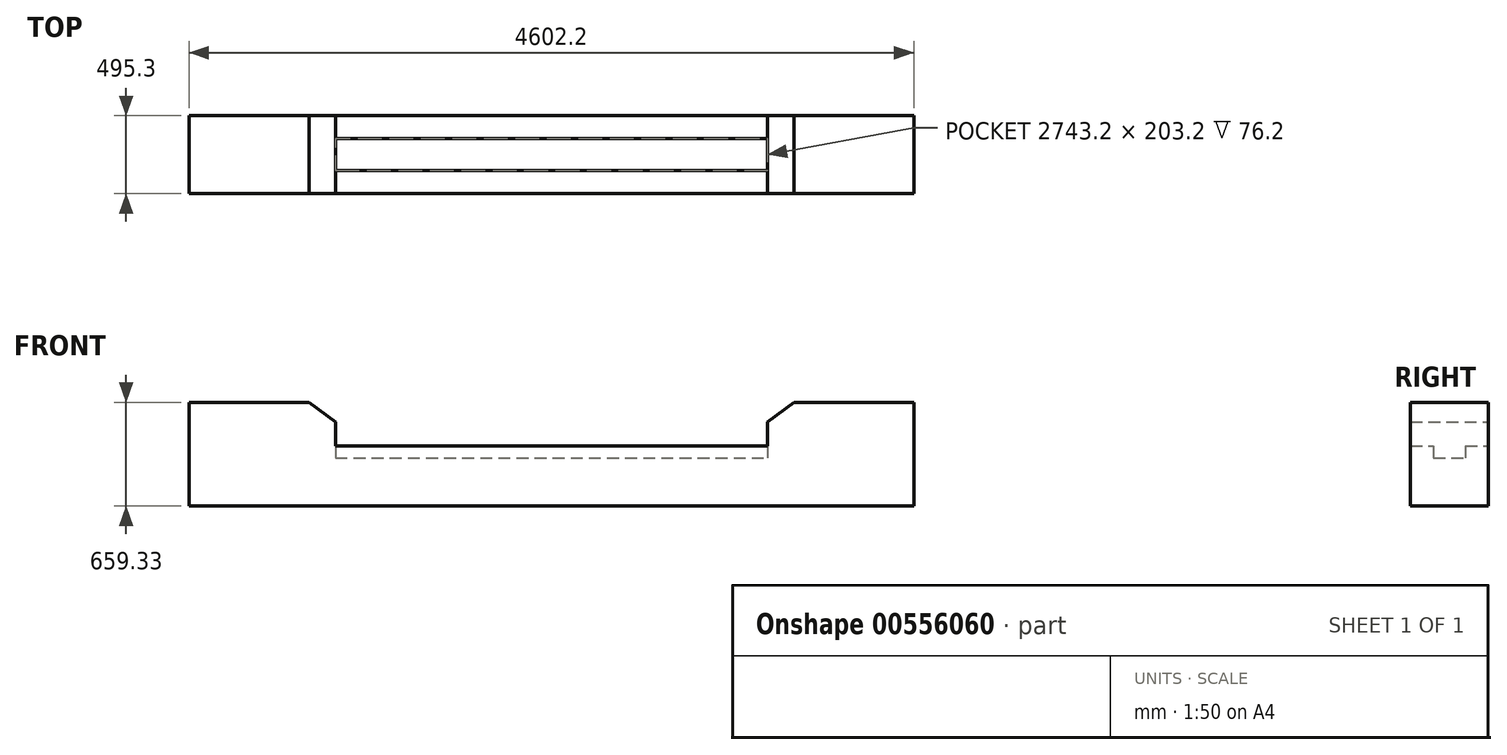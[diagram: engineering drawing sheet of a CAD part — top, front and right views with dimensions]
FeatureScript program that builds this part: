
annotation { "Feature Type Name" : "Feature", "Feature Type Description" : "" }
export const myFeature = defineFeature(function(context is Context, id is Id, definition is map)
    precondition{}
    {
        {
            var Q0;
            Q0=qCreatedBy(makeId("Front.planeOp"),FACE);
            var sketch = newSketch(context, id + "F0", { "sketchPlane" : qUnion([Q0])});
            skLineSegment(sketch, "E0", {"start": v(0, 0) * mm, "end": v(1371.6, 0) * mm});
            skLineSegment(sketch, "E1", {"start": v(1371.6, 0) * mm, "end": v(1371.6, -127) * mm});
            skLineSegment(sketch, "E2", {"start": v(1371.6, -127) * mm, "end": v(-1371.6, -127) * mm});
            skLineSegment(sketch, "E3", {"start": v(-1371.6, -127) * mm, "end": v(-1371.6, 0) * mm});
            skLineSegment(sketch, "E4", {"start": v(-1371.6, 0) * mm, "end": v(0, 0) * mm});
            skLineSegment(sketch, "E5", {"start": v(-1371.6, 101.6) * mm, "end": v(-1539.1, 227.53) * mm});
            skLineSegment(sketch, "E6", {"start": v(-1539.1, 227.53) * mm, "end": v(-2301.1, 227.53) * mm});
            skLineSegment(sketch, "E7", {"start": v(-2301.1, 227.53) * mm, "end": v(-2301.1, -229.67) * mm});
            skLineSegment(sketch, "E8", {"start": v(0, -127) * mm, "end": v(0, -431.8) * mm});
            skPoint(sketch, "E8.endSnap0", {"position": v(0, -127) * mm});
            skLineSegment(sketch, "E9", {"start": v(0, -431.8) * mm, "end": v(-2301.1, -431.8) * mm});
            skLineSegment(sketch, "E10", {"start": v(-2301.1, -431.8) * mm, "end": v(-2301.1, -229.67) * mm});
            skLineSegment(sketch, "E11.MirrorCS", {"start": v(0, -431.8) * mm, "end": v(2301.1, -431.8) * mm});
            skLineSegment(sketch, "E12.MirrorCS", {"start": v(2301.1, 227.53) * mm, "end": v(2301.1, -229.67) * mm});
            skLineSegment(sketch, "E13.MirrorCS", {"start": v(2301.1, -431.8) * mm, "end": v(2301.1, -229.67) * mm});
            skLineSegment(sketch, "E14.MirrorCS", {"start": v(1539.1, 227.53) * mm, "end": v(2301.1, 227.53) * mm});
            skLineSegment(sketch, "E15.MirrorCS", {"start": v(1371.6, 101.6) * mm, "end": v(1539.1, 227.53) * mm});
            skLineSegment(sketch, "E16.MirrorCS", {"start": v(1371.6, 0) * mm, "end": v(1371.6, 101.6) * mm});
            skLineSegment(sketch, "E17", {"start": v(-1371.6, 0) * mm, "end": v(-1371.6, 101.6) * mm});
            skSolve(sketch);
        }
        {
            var Q0;
            {var subQ0=sQuery(id+"F0.wireOp",EDGE,"E3");Q0=makeQuery(id+"F0.imprint","IMPRINT",FACE,{"disambiguationData":[TD([[makeQuery(id+"F0.imprint","IMPRINT",EDGE,{"derivedFrom":subQ0}),1.0]])]});}
            var Q1;
            {var subQ1=sQuery(id+"F0.wireOp",EDGE,"E1");Q1=makeQuery(id+"F0.imprint","IMPRINT",FACE,{"disambiguationData":[TD([[makeQuery(id+"F0.imprint","IMPRINT",EDGE,{"derivedFrom":subQ1}),1.0]])]});}
            extrude(context, id + "F1", {"entities" : qUnion([Q0, Q1]), "depth" : 349.25 * mm, "offsetDistance" : 25.4 * mm});
        }
        {
            var Q0;
            Q0=makeQuery(id+"F1.opExtrude","CAP_FACE",FACE,{"disambiguationData":[OSD([sQuery(id+"F0.wireOp",EDGE,"E1"),sQuery(id+"F0.wireOp",EDGE,"E2"),sQuery(id+"F0.wireOp",EDGE,"E3"),sQuery(id+"F0.wireOp",EDGE,"E5"),sQuery(id+"F0.wireOp",EDGE,"E6"),sQuery(id+"F0.wireOp",EDGE,"E7"),sQuery(id+"F0.wireOp",EDGE,"E9"),sQuery(id+"F0.wireOp",EDGE,"E10"),sQuery(id+"F0.wireOp",EDGE,"E11.MirrorCS"),sQuery(id+"F0.wireOp",EDGE,"E12.MirrorCS"),sQuery(id+"F0.wireOp",EDGE,"E13.MirrorCS"),sQuery(id+"F0.wireOp",EDGE,"E14.MirrorCS"),sQuery(id+"F0.wireOp",EDGE,"E15.MirrorCS"),sQuery(id+"F0.wireOp",EDGE,"E16.MirrorCS"),sQuery(id+"F0.wireOp",EDGE,"E17")])],"isStart":true});
            extrude(context, id + "F2", {"entities" : qUnion([Q0]), "operationType" : NewBodyOperationType.ADD, "depth" : 146.05 * mm, "offsetDistance" : 25.4 * mm});
        }
        {
            var Q0;
            {var subQ0=sQuery(id+"F0.wireOp",EDGE,"E2");Q0=makeQuery(id+"F2.boolean.opBoolean","MERGE",FACE,{"derivedFrom":[makeQuery(id+"F1.opExtrude","SWEPT_FACE",FACE,{"disambiguationData":[OSD([subQ0])]}),makeQuery(id+"F2.opExtrude","SWEPT_FACE",FACE,{"disambiguationData":[OSD([subQ0])]})]});}
            var sketch = newSketch(context, id + "F3", { "sketchPlane" : qUnion([Q0])});
            skPoint(sketch, "E18.end.orphan", {"position": v(-1371.6, -101.6) * mm});
            skPoint(sketch, "E19.start.orphan", {"position": v(-791.9, 146.05) * mm});
            skLineSegment(sketch, "E20", {"start": v(1371.6, 146.05) * mm, "end": v(1371.6, 0) * mm});
            skLineSegment(sketch, "E21", {"start": v(-1369.65, 0) * mm, "end": v(1371.6, 0) * mm});
            skLineSegment(sketch, "E22", {"start": v(-1369.65, 0) * mm, "end": v(-1371.6, 0) * mm});
            skLineSegment(sketch, "E23", {"start": v(-1371.6, 0) * mm, "end": v(-1371.6, 146.05) * mm});
            skLineSegment(sketch, "E24", {"start": v(-1371.6, 146.05) * mm, "end": v(-791.9, 146.05) * mm});
            skLineSegment(sketch, "E25.MirrorCS", {"start": v(-1369.65, -203.2) * mm, "end": v(1371.6, -203.2) * mm});
            skLineSegment(sketch, "E26.MirrorCS", {"start": v(-1371.6, -349.25) * mm, "end": v(-791.9, -349.25) * mm});
            skLineSegment(sketch, "E27", {"start": v(-791.9, 146.05) * mm, "end": v(1371.6, 146.05) * mm});
            skLineSegment(sketch, "E28", {"start": v(1371.6, 0) * mm, "end": v(1371.6, 146.05) * mm});
            skLineSegment(sketch, "E29.MirrorCS", {"start": v(-791.9, -349.25) * mm, "end": v(1371.6, -349.25) * mm});
            skLineSegment(sketch, "E30", {"start": v(-1371.6, -101.6) * mm, "end": v(-1052.12, -101.6) * mm});
            skLineSegment(sketch, "E31.MirrorCS", {"start": v(-1371.6, -203.2) * mm, "end": v(-1371.6, -349.25) * mm});
            skLineSegment(sketch, "E32.MirrorCS", {"start": v(1371.6, -203.2) * mm, "end": v(1371.6, -349.25) * mm});
            skLineSegment(sketch, "E33", {"start": v(-1371.6, -203.2) * mm, "end": v(-1369.65, -203.2) * mm});
            skSolve(sketch);
        }
        {
            var Q0;
            Q0=makeQuery(id+"F3.imprint","IMPRINT",FACE,{"disambiguationData":[TD([[makeQuery(id+"F3.imprint","IMPRINT",EDGE,{"derivedFrom":sQuery(id+"F3.wireOp",EDGE,"E26.MirrorCS")}),-1.0]])]});
            var Q1;
            Q1=makeQuery(id+"F3.imprint","IMPRINT",FACE,{"disambiguationData":[TD([[makeQuery(id+"F3.imprint","IMPRINT",EDGE,{"derivedFrom":sQuery(id+"F3.wireOp",EDGE,"E21")}),1.0]])]});
            extrude(context, id + "F4", {"entities" : qUnion([Q0, Q1]), "operationType" : NewBodyOperationType.ADD, "depth" : 76.2 * mm, "offsetDistance" : 25.4 * mm});
        }
    });
